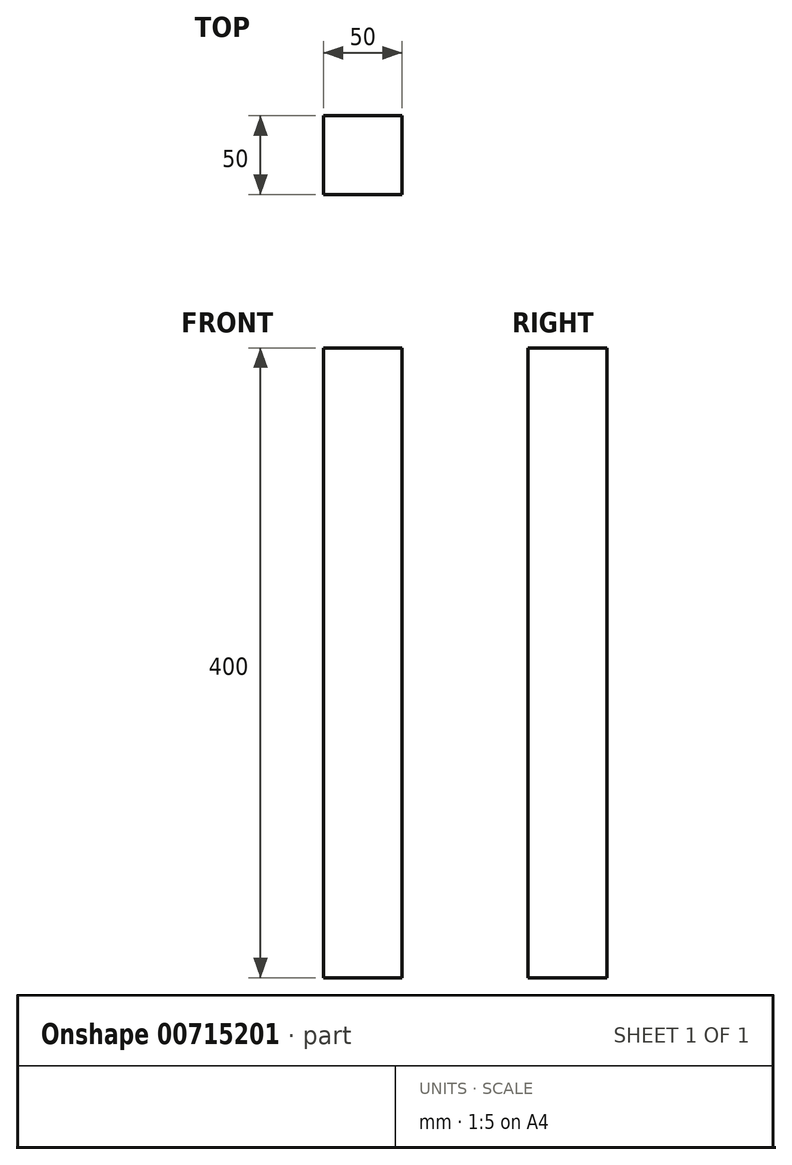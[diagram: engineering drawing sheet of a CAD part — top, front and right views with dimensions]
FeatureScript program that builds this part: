
annotation { "Feature Type Name" : "Feature", "Feature Type Description" : "" }
export const myFeature = defineFeature(function(context is Context, id is Id, definition is map)
    precondition{}
    {
        {
            var Q0;
            Q0=qCreatedBy(makeId("Top.planeOp"),FACE);
            var sketch = newSketch(context, id + "F0", { "sketchPlane" : qUnion([Q0])});
            skLineSegment(sketch, "E0.bottom", {"start": v(25, 25) * mm, "end": v(-25, 25) * mm});
            skLineSegment(sketch, "E0.top", {"start": v(25, -25) * mm, "end": v(-25, -25) * mm});
            skLineSegment(sketch, "E0.left", {"start": v(25, 25) * mm, "end": v(25, -25) * mm});
            skLineSegment(sketch, "E0.right", {"start": v(-25, 25) * mm, "end": v(-25, -25) * mm});
            skPoint(sketch, "E0.middle", {"position": v(0, 0) * mm});
            skSolve(sketch);
        }
        {
            var Q0;
            Q0=makeQuery(id+"F0.imprint","IMPRINT",FACE,{"disambiguationData":[TD([[makeQuery(id+"F0.imprint","IMPRINT",EDGE,{"derivedFrom":sQuery(id+"F0.wireOp",EDGE,"E0.bottom")}),1.0]])]});
            extrude(context, id + "F1", {"entities" : qUnion([Q0]), "depth" : 400 * mm, "offsetDistance" : 25 * mm});
        }
    });
